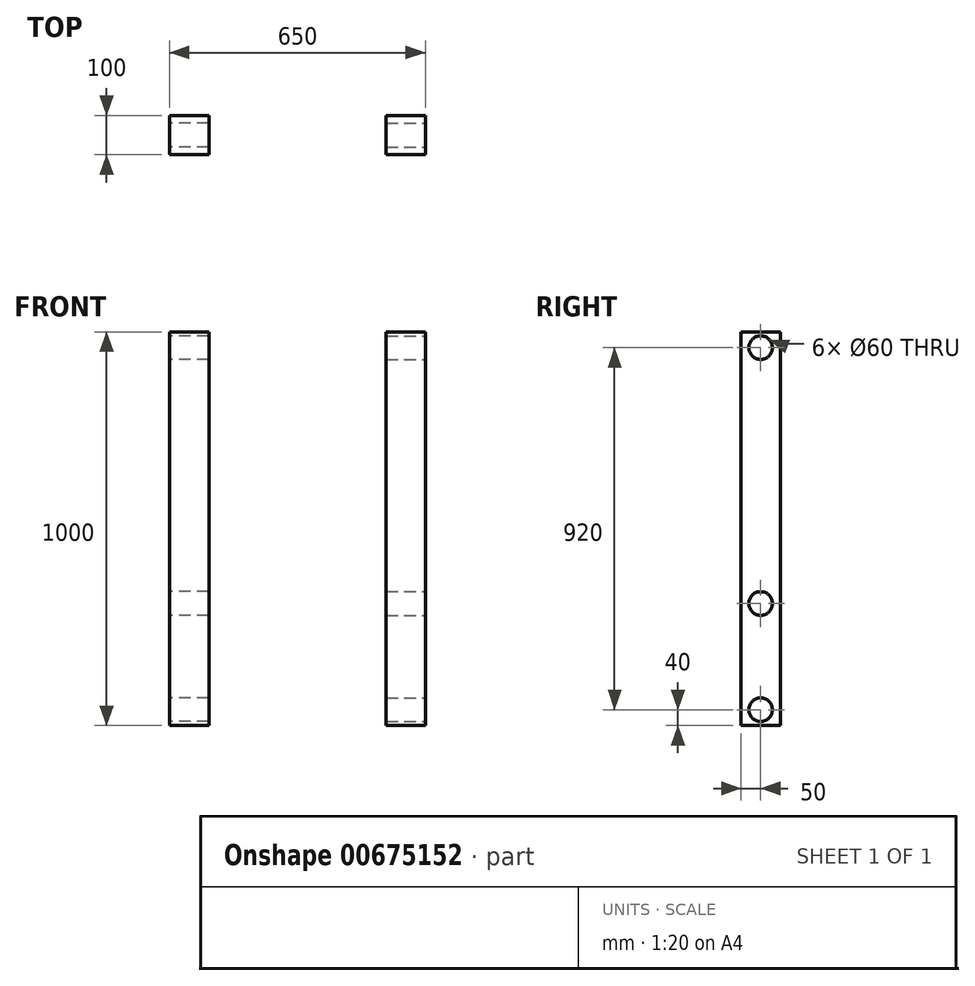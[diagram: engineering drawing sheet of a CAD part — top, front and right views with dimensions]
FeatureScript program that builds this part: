
annotation { "Feature Type Name" : "Feature", "Feature Type Description" : "" }
export const myFeature = defineFeature(function(context is Context, id is Id, definition is map)
    precondition{}
    {
        {
            var Q0;
            Q0=qCreatedBy(makeId("Top.planeOp"),FACE);
            var sketch = newSketch(context, id + "F0", { "sketchPlane" : qUnion([Q0])});
            skLineSegment(sketch, "E0.bottom", {"start": v(-325, 50) * mm, "end": v(-225, 50) * mm});
            skLineSegment(sketch, "E0.top", {"start": v(-325, -50) * mm, "end": v(-225, -50) * mm});
            skLineSegment(sketch, "E0.left", {"start": v(-325, 50) * mm, "end": v(-325, -50) * mm});
            skLineSegment(sketch, "E0.right", {"start": v(-225, 50) * mm, "end": v(-225, -50) * mm});
            skLineSegment(sketch, "E1.bottom", {"start": v(225, 50) * mm, "end": v(325, 50) * mm});
            skLineSegment(sketch, "E1.top", {"start": v(225, -50) * mm, "end": v(325, -50) * mm});
            skLineSegment(sketch, "E1.left", {"start": v(225, 50) * mm, "end": v(225, -50) * mm});
            skLineSegment(sketch, "E1.right", {"start": v(325, 50) * mm, "end": v(325, -50) * mm});
            skSolve(sketch);
        }
        {
            var Q0;
            Q0=makeQuery(id+"F0.imprint","IMPRINT",FACE,{"disambiguationData":[TD([[makeQuery(id+"F0.imprint","IMPRINT",EDGE,{"derivedFrom":sQuery(id+"F0.wireOp",EDGE,"E0.bottom")}),-1.0]])]});
            var Q1;
            Q1=makeQuery(id+"F0.imprint","IMPRINT",FACE,{"disambiguationData":[TD([[makeQuery(id+"F0.imprint","IMPRINT",EDGE,{"derivedFrom":sQuery(id+"F0.wireOp",EDGE,"E1.bottom")}),-1.0]])]});
            extrude(context, id + "F1", {"entities" : qUnion([Q0, Q1]), "depth" : 1000 * mm, "offsetDistance" : 25 * mm});
        }
        {
            var Q0;
            Q0=makeQuery(id+"F1.opExtrude","SWEPT_FACE",FACE,{"disambiguationData":[OSD([sQuery(id+"F0.wireOp",EDGE,"E0.left")])]});
            var sketch = newSketch(context, id + "F2", { "sketchPlane" : qUnion([Q0])});
            skCircle(sketch, "E2", {"center": v(0, 960) * mm, "radius": 30 * mm});
            skSolve(sketch);
        }
        {
            var Q0;
            Q0 = qSketchRegion(id + "F2", true);
            extrude(context, id + "F3", {"entities" : qUnion([Q0]), "operationType" : NewBodyOperationType.REMOVE, "oppositeDirection" : true, "depth" : 100 * mm, "offsetDistance" : 25 * mm});
        }
        {
            var Q0;
            Q0=makeQuery(id+"F1.opExtrude","SWEPT_FACE",FACE,{"disambiguationData":[OSD([sQuery(id+"F0.wireOp",EDGE,"E0.left")])]});
            var sketch = newSketch(context, id + "F4", { "sketchPlane" : qUnion([Q0])});
            skCircle(sketch, "E3", {"center": v(0, 40) * mm, "radius": 30 * mm});
            skSolve(sketch);
        }
        {
            var Q0;
            Q0=makeQuery(id+"F4.imprint","IMPRINT",FACE,{"disambiguationData":[TD([[makeQuery(id+"F4.imprint","IMPRINT",EDGE,{"derivedFrom":sQuery(id+"F4.wireOp",EDGE,"E3")}),1.0]])]});
            extrude(context, id + "F5", {"entities" : qUnion([Q0]), "operationType" : NewBodyOperationType.REMOVE, "oppositeDirection" : true, "depth" : 100 * mm, "offsetDistance" : 25 * mm});
        }
        {
            var Q0;
            Q0=makeQuery(id+"F1.opExtrude","SWEPT_FACE",FACE,{"disambiguationData":[OSD([sQuery(id+"F0.wireOp",EDGE,"E1.right")])]});
            var sketch = newSketch(context, id + "F6", { "sketchPlane" : qUnion([Q0])});
            skCircle(sketch, "E4", {"center": v(0, 960) * mm, "radius": 30 * mm});
            skSolve(sketch);
        }
        {
            var Q0;
            Q0=makeQuery(id+"F6.imprint","IMPRINT",FACE,{"disambiguationData":[TD([[makeQuery(id+"F6.imprint","IMPRINT",EDGE,{"derivedFrom":sQuery(id+"F6.wireOp",EDGE,"E4")}),1.0]])]});
            extrude(context, id + "F7", {"entities" : qUnion([Q0]), "operationType" : NewBodyOperationType.REMOVE, "oppositeDirection" : true, "depth" : 100 * mm, "offsetDistance" : 25 * mm});
        }
        {
            var Q0;
            Q0=makeQuery(id+"F1.opExtrude","SWEPT_FACE",FACE,{"disambiguationData":[OSD([sQuery(id+"F0.wireOp",EDGE,"E1.right")])]});
            var sketch = newSketch(context, id + "F8", { "sketchPlane" : qUnion([Q0])});
            skCircle(sketch, "E5", {"center": v(0, 40) * mm, "radius": 30 * mm});
            skSolve(sketch);
        }
        {
            var Q0;
            Q0=makeQuery(id+"F8.imprint","IMPRINT",FACE,{"disambiguationData":[TD([[makeQuery(id+"F8.imprint","IMPRINT",EDGE,{"derivedFrom":sQuery(id+"F8.wireOp",EDGE,"E5")}),1.0]])]});
            extrude(context, id + "F9", {"entities" : qUnion([Q0]), "operationType" : NewBodyOperationType.REMOVE, "oppositeDirection" : true, "depth" : 100 * mm, "offsetDistance" : 25 * mm});
        }
        {
            var Q0;
            Q0=makeQuery(id+"F1.opExtrude","SWEPT_FACE",FACE,{"disambiguationData":[OSD([sQuery(id+"F0.wireOp",EDGE,"E1.right")])]});
            var sketch = newSketch(context, id + "F10", { "sketchPlane" : qUnion([Q0])});
            skCircle(sketch, "E6", {"center": v(0, 310) * mm, "radius": 30 * mm});
            skSolve(sketch);
        }
        {
            var Q0;
            Q0=makeQuery(id+"F10.imprint","IMPRINT",FACE,{"disambiguationData":[TD([[makeQuery(id+"F10.imprint","IMPRINT",EDGE,{"derivedFrom":sQuery(id+"F10.wireOp",EDGE,"E6")}),1.0]])]});
            extrude(context, id + "F11", {"entities" : qUnion([Q0]), "operationType" : NewBodyOperationType.REMOVE, "oppositeDirection" : true, "depth" : 100 * mm, "offsetDistance" : 25 * mm});
        }
        {
            var Q0;
            Q0=makeQuery(id+"F1.opExtrude","SWEPT_FACE",FACE,{"disambiguationData":[OSD([sQuery(id+"F0.wireOp",EDGE,"E0.left")])]});
            var sketch = newSketch(context, id + "F12", { "sketchPlane" : qUnion([Q0])});
            skCircle(sketch, "E7", {"center": v(0, 310) * mm, "radius": 30 * mm});
            skSolve(sketch);
        }
        {
            var Q0;
            Q0=makeQuery(id+"F12.imprint","IMPRINT",FACE,{"disambiguationData":[TD([[makeQuery(id+"F12.imprint","IMPRINT",EDGE,{"derivedFrom":sQuery(id+"F12.wireOp",EDGE,"E7")}),1.0]])]});
            extrude(context, id + "F13", {"entities" : qUnion([Q0]), "operationType" : NewBodyOperationType.REMOVE, "oppositeDirection" : true, "depth" : 100 * mm, "offsetDistance" : 25 * mm});
        }
    });
